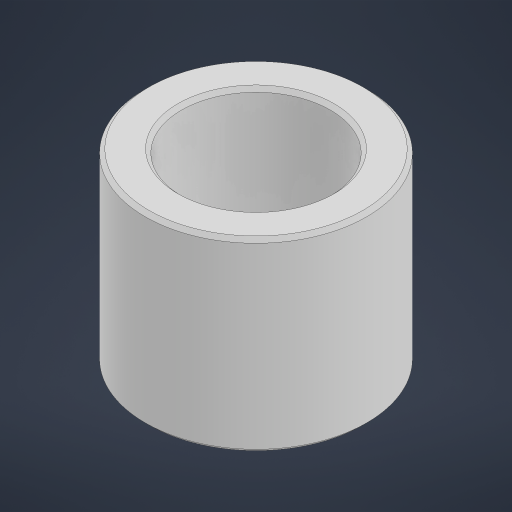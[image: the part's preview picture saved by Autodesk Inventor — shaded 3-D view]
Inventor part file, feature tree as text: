
AUTODESK INVENTOR PART (.ipt)
format: ipt  version: 2023 (Build 270158000, 158)  size: 172,032 bytes
history: native  units: in
note: dims shown in document units (in); Inventor stores cm internally (conversion verified against a paired STEP export)
features: chamfer x1
ambient origin geometry x8: Origin, YZ Plane, XZ Plane, XY Plane, X Axis, Y Axis, Z Axis, Center Point
bodies: Solid1 (feature_tree)
feature tree (1):
  chamfer  "Chamfer1"  [1 undecoded]
note: 1 required parameter value undecoded (feature->parameter linkage not recoverable at this tier; creation-order binding heuristic only, values carry confidence <= 0.55)
